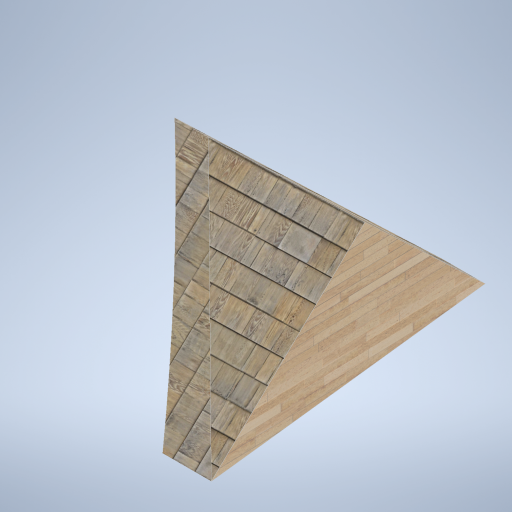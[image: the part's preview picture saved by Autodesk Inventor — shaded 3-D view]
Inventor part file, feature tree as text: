
AUTODESK INVENTOR PART (.ipt)
format: ipt  version: 2024.2 (Build 282272000, 272)  size: 520,192 bytes
history: native  units: mm
features: sketch x8, plane x6, extrude x3, loft x2, projected_geometry x2, other x1
ambient origin geometry x8: Origin, YZ Plane, XZ Plane, XY Plane, X Axis, Y Axis, Z Axis, Center Point
bodies: Solid1 (feature_tree)
feature tree (22):
  sketch  "Sketch1"  dims[d5=0.0mm d6=-7900.0mm d7=800.0mm]
  plane  "Work Plane2"
  loft  "Loft1"
  plane  "Work Plane3"
  extrude  "Extrusion1"  Depth=9000.0mm
  plane  "Work Plane4"
  sketch  "Sketch5"  dims[d12=800.0mm d13=0.0mm d14=90.0deg]
  plane  "Work Plane5"
  extrude  "Extrusion2"  Depth=9000.0mm
  plane  "Work Plane6"
  sketch  "Sketch7"  dims[d18=0.0mm d19=0.0mm]
  loft  "Loft2"
  extrude  "Extrusion3"  Depth=2500.0mm
  plane  "Work Plane1"
  sketch  "Sketch2"  dims[d8=9000.0mm d9=9000.0mm]
  sketch  "Sketch3"  dims[d10=9000.0mm d11=9000.0mm]
  sketch  "Sketch6"  dims[d15=0.0mm d16=90.0deg d17=2500.0mm]
  projected_geometry  "Projected Loop1"
  sketch  "Sketch8"  dims[d20=0.0mm]
  projected_geometry  "Projected Loop2"
  other  "Edges1"
  sketch  "Sketch9"  dims[d21=6.981317mm d22=0.0mm d23=0.0mm d24=90.0deg d25=0.0mm d26=90.0deg d27=0.0mm d28=90.0deg d29=1.0mm d30=0.0mm]
